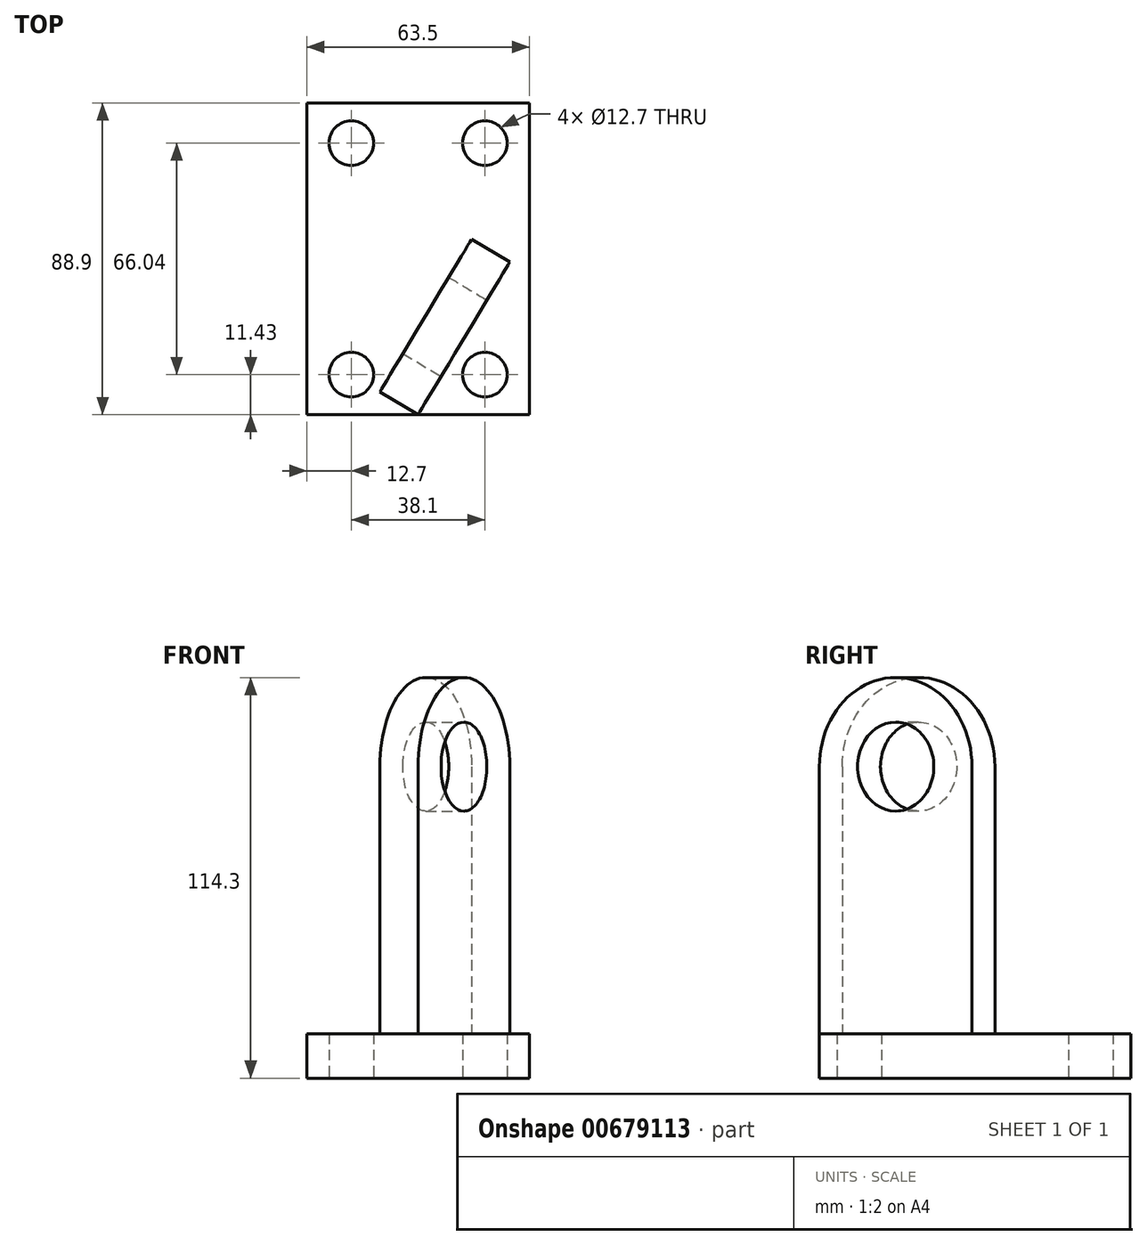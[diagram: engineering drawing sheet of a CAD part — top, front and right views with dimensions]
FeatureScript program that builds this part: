
annotation { "Feature Type Name" : "Feature", "Feature Type Description" : "" }
export const myFeature = defineFeature(function(context is Context, id is Id, definition is map)
    precondition{}
    {
        {
            var Q0;
            Q0=qCreatedBy(makeId("Top.planeOp"),FACE);
            var sketch = newSketch(context, id + "F0", { "sketchPlane" : qUnion([Q0])});
            skLineSegment(sketch, "E0", {"start": v(0, 0) * mm, "end": v(0, 88.9) * mm});
            skLineSegment(sketch, "E1", {"start": v(0, 88.9) * mm, "end": v(63.5, 88.9) * mm});
            skLineSegment(sketch, "E2", {"start": v(63.5, 88.9) * mm, "end": v(63.5, 0) * mm});
            skLineSegment(sketch, "E3", {"start": v(63.5, 0) * mm, "end": v(0, 0) * mm});
            skCircle(sketch, "E4", {"center": v(12.7, 77.47) * mm, "radius": 6.35 * mm});
            skCircle(sketch, "E5", {"center": v(50.8, 77.47) * mm, "radius": 6.35 * mm});
            skCircle(sketch, "E6", {"center": v(50.8, 11.43) * mm, "radius": 6.35 * mm});
            skCircle(sketch, "E7", {"center": v(12.7, 11.43) * mm, "radius": 6.35 * mm});
            skLineSegment(sketch, "E8", {"start": v(31.75, 0) * mm, "end": v(57.91, 43.54) * mm});
            skLineSegment(sketch, "E9.0", {"start": v(20.86, 6.54) * mm, "end": v(47.03, 50.09) * mm});
            skLineSegment(sketch, "E10", {"start": v(47.03, 50.09) * mm, "end": v(57.91, 43.54) * mm});
            skLineSegment(sketch, "E11", {"start": v(31.75, 0) * mm, "end": v(20.86, 6.54) * mm});
            skSolve(sketch);
        }
        {
            var Q0;
            {var subQ2=sQuery(id+"F0.wireOp",EDGE,"E0");Q0=makeQuery(id+"F0.imprint","IMPRINT",FACE,{"disambiguationData":[TD([[makeQuery(id+"F0.imprint","IMPRINT",EDGE,{"derivedFrom":subQ2}),-1.0]])]});}
            var Q1;
            Q1=makeQuery(id+"F0.imprint","IMPRINT",FACE,{"disambiguationData":[TD([[makeQuery(id+"F0.imprint","IMPRINT",EDGE,{"derivedFrom":sQuery(id+"F0.wireOp",EDGE,"E5")}),1.0]])]});
            var Q2;
            Q2=makeQuery(id+"F0.imprint","IMPRINT",FACE,{"disambiguationData":[TD([[makeQuery(id+"F0.imprint","IMPRINT",EDGE,{"derivedFrom":sQuery(id+"F0.wireOp",EDGE,"E4")}),1.0]])]});
            var Q3;
            Q3=makeQuery(id+"F0.imprint","IMPRINT",FACE,{"disambiguationData":[TD([[makeQuery(id+"F0.imprint","IMPRINT",EDGE,{"derivedFrom":sQuery(id+"F0.wireOp",EDGE,"E8")}),1.0]])]});
            var Q4;
            Q4=makeQuery(id+"F0.imprint","IMPRINT",FACE,{"disambiguationData":[TD([[makeQuery(id+"F0.imprint","IMPRINT",EDGE,{"derivedFrom":sQuery(id+"F0.wireOp",EDGE,"E6")}),1.0]])]});
            var Q5;
            Q5=makeQuery(id+"F0.imprint","IMPRINT",FACE,{"disambiguationData":[TD([[makeQuery(id+"F0.imprint","IMPRINT",EDGE,{"derivedFrom":sQuery(id+"F0.wireOp",EDGE,"E7")}),1.0]])]});
            extrude(context, id + "F1", {"entities" : qUnion([Q0, Q1, Q2, Q3, Q4, Q5]), "depth" : 12.7 * mm, "offsetDistance" : 25.4 * mm});
        }
        {
            var Q0;
            Q0=makeQuery(id+"F0.imprint","IMPRINT",FACE,{"disambiguationData":[TD([[makeQuery(id+"F0.imprint","IMPRINT",EDGE,{"derivedFrom":sQuery(id+"F0.wireOp",EDGE,"E8")}),1.0]])]});
            extrude(context, id + "F2", {"entities" : qUnion([Q0]), "operationType" : NewBodyOperationType.ADD, "depth" : 114.3 * mm, "offsetDistance" : 25.4 * mm});
        }
        {
            var Q0;
            Q0=makeQuery(id+"F2.opExtrude","SWEPT_FACE",FACE,{"disambiguationData":[OSD([sQuery(id+"F0.wireOp",EDGE,"E8")])]});
            var sketch = newSketch(context, id + "F3", { "sketchPlane" : qUnion([Q0])});
            skCircle(sketch, "E12", {"center": v(41.75, 88.9) * mm, "radius": 12.7 * mm});
            skLineSegment(sketch, "E13", {"start": v(16.35, 12.7) * mm, "end": v(16.35, 88.9) * mm});
            skLineSegment(sketch, "E14", {"start": v(41.75, 114.3) * mm, "end": v(41.75, 114.3) * mm});
            skLineSegment(sketch, "E15", {"start": v(67.15, 88.9) * mm, "end": v(67.15, 12.7) * mm});
            skLineSegment(sketch, "E16", {"start": v(67.15, 12.7) * mm, "end": v(16.35, 12.7) * mm});
            skPoint(sketch, "E17.visualSharp", {"position": v(16.35, 114.3) * mm});
            skArc(sketch, "E17.filletArc", {"start": v(41.75, 114.3) * mm, "mid": v(23.8, 106.86) * mm, "end": v(16.35, 88.9) * mm});
            skPoint(sketch, "E18.visualSharp", {"position": v(67.15, 114.3) * mm});
            skArc(sketch, "E18.filletArc", {"start": v(67.15, 88.9) * mm, "mid": v(59.71, 106.86) * mm, "end": v(41.75, 114.3) * mm});
            skSolve(sketch);
        }
        {
            var Q0;
            {var subQ0=sQuery(id+"F3.wireOp",EDGE,"E17.filletArc");Q0=makeQuery(id+"F3.imprint","IMPRINT",FACE,{"disambiguationData":[TD([[makeQuery(id+"F3.imprint","IMPRINT",EDGE,{"derivedFrom":subQ0}),-1.0]])]});}
            var Q1;
            {var subQ0=sQuery(id+"F3.wireOp",EDGE,"E18.filletArc");Q1=makeQuery(id+"F3.imprint","IMPRINT",FACE,{"disambiguationData":[TD([[makeQuery(id+"F3.imprint","IMPRINT",EDGE,{"derivedFrom":subQ0}),-1.0]])]});}
            extrude(context, id + "F4", {"entities" : qUnion([Q0, Q1]), "operationType" : NewBodyOperationType.REMOVE, "endBound" : BoundingType.THROUGH_ALL, "oppositeDirection" : true, "depth" : 25.4 * mm, "offsetDistance" : 25.4 * mm});
        }
        {
            var Q0;
            Q0=makeQuery(id+"F3.imprint","IMPRINT",FACE,{"disambiguationData":[TD([[makeQuery(id+"F3.imprint","IMPRINT",EDGE,{"derivedFrom":sQuery(id+"F3.wireOp",EDGE,"E12")}),1.0]])]});
            extrude(context, id + "F5", {"entities" : qUnion([Q0]), "operationType" : NewBodyOperationType.REMOVE, "endBound" : BoundingType.THROUGH_ALL, "oppositeDirection" : true, "depth" : 25.4 * mm, "offsetDistance" : 25.4 * mm});
        }
        {
            var Q0;
            Q0=makeQuery(id+"F0.imprint","IMPRINT",FACE,{"disambiguationData":[TD([[makeQuery(id+"F0.imprint","IMPRINT",EDGE,{"derivedFrom":sQuery(id+"F0.wireOp",EDGE,"E6")}),1.0]])]});
            var Q1;
            Q1=makeQuery(id+"F0.imprint","IMPRINT",FACE,{"disambiguationData":[TD([[makeQuery(id+"F0.imprint","IMPRINT",EDGE,{"derivedFrom":sQuery(id+"F0.wireOp",EDGE,"E5")}),1.0]])]});
            var Q2;
            Q2=makeQuery(id+"F0.imprint","IMPRINT",FACE,{"disambiguationData":[TD([[makeQuery(id+"F0.imprint","IMPRINT",EDGE,{"derivedFrom":sQuery(id+"F0.wireOp",EDGE,"E4")}),1.0]])]});
            var Q3;
            Q3=makeQuery(id+"F0.imprint","IMPRINT",FACE,{"disambiguationData":[TD([[makeQuery(id+"F0.imprint","IMPRINT",EDGE,{"derivedFrom":sQuery(id+"F0.wireOp",EDGE,"E7")}),1.0]])]});
            extrude(context, id + "F6", {"entities" : qUnion([Q0, Q1, Q2, Q3]), "operationType" : NewBodyOperationType.REMOVE, "endBound" : BoundingType.THROUGH_ALL, "depth" : 50.04 * mm, "offsetDistance" : 25.4 * mm});
        }
    });
